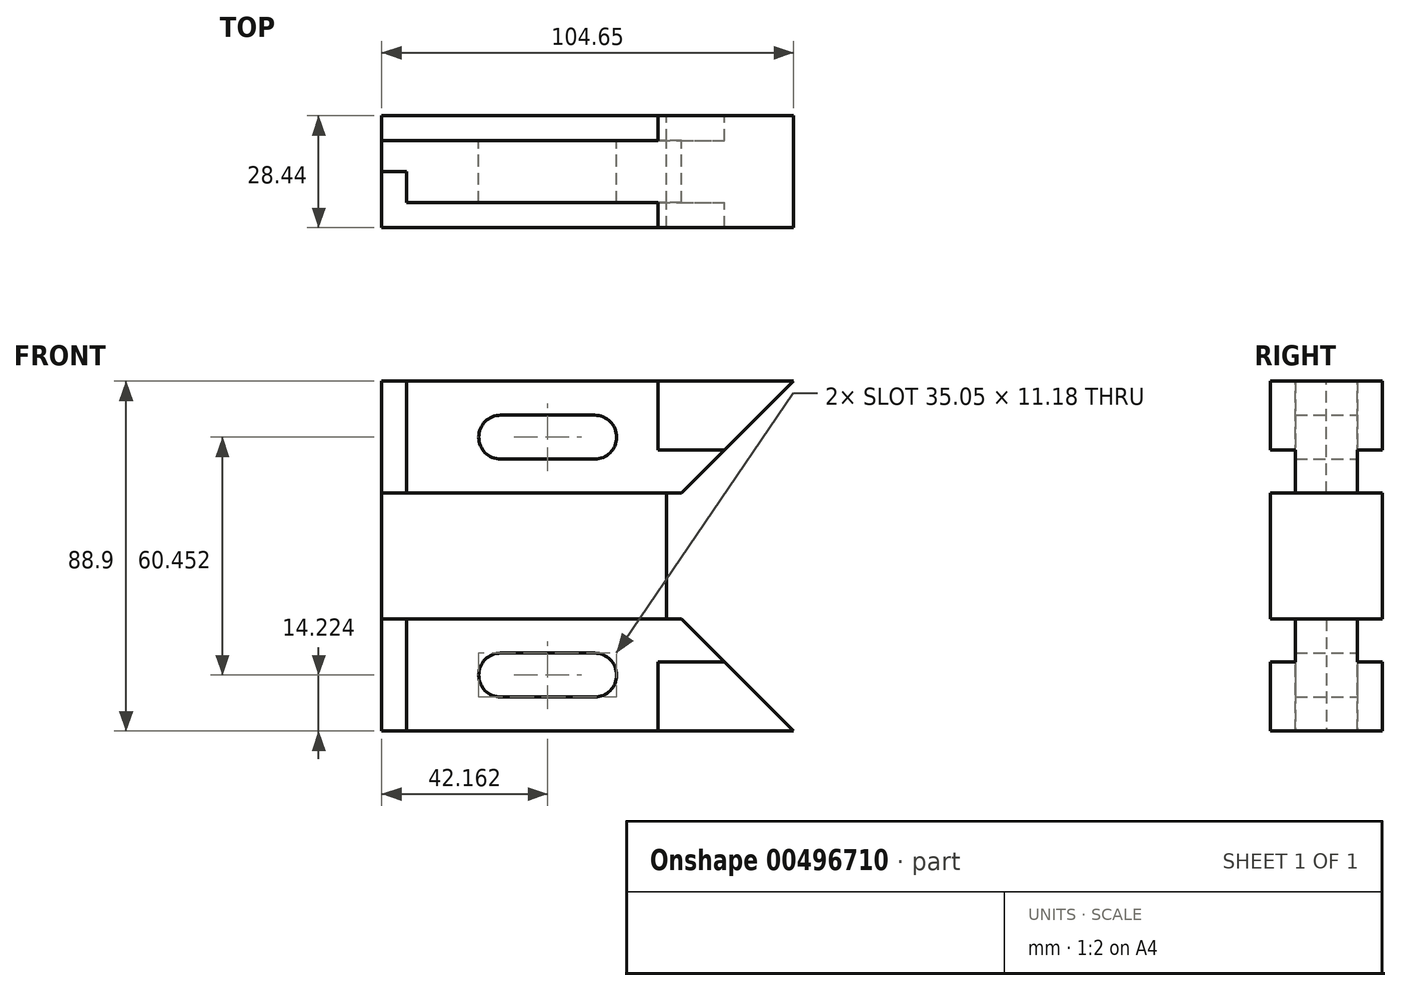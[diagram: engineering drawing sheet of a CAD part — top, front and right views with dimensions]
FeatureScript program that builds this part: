
annotation { "Feature Type Name" : "Feature", "Feature Type Description" : "" }
export const myFeature = defineFeature(function(context is Context, id is Id, definition is map)
    precondition{}
    {
        {
            var Q0;
            Q0=qCreatedBy(makeId("Front.planeOp"),FACE);
            var sketch = newSketch(context, id + "F0", { "sketchPlane" : qUnion([Q0])});
            skLineSegment(sketch, "E0.MirrorCS", {"start": v(-0.76, 16) * mm, "end": v(-76.96, 16) * mm});
            skLineSegment(sketch, "E1.MirrorCS", {"start": v(-76.96, 16) * mm, "end": v(-76.96, 44.45) * mm});
            skLineSegment(sketch, "E2.MirrorCS", {"start": v(-0.76, 16) * mm, "end": v(27.69, 44.45) * mm});
            skLineSegment(sketch, "E3.MirrorCS", {"start": v(-70.61, 16) * mm, "end": v(-70.61, 44.45) * mm});
            skLineSegment(sketch, "E4.MirrorCS", {"start": v(-76.96, 44.45) * mm, "end": v(27.69, 44.45) * mm});
            skLineSegment(sketch, "E5", {"start": v(-76.96, 30.23) * mm, "end": v(-76.96, 30.23) * mm});
            skPoint(sketch, "E5.endSnap0", {"position": v(-76.96, 30.23) * mm});
            skArc(sketch, "E6", {"start": v(-22.86, 24.64) * mm, "mid": v(-17.27, 30.23) * mm, "end": v(-22.86, 35.81) * mm});
            skArc(sketch, "E7", {"start": v(-46.74, 35.81) * mm, "mid": v(-52.32, 30.23) * mm, "end": v(-46.74, 24.64) * mm});
            skLineSegment(sketch, "E8", {"start": v(-46.74, 35.81) * mm, "end": v(-22.86, 35.81) * mm});
            skLineSegment(sketch, "E9", {"start": v(-22.86, 24.64) * mm, "end": v(-46.74, 24.64) * mm});
            skLineSegment(sketch, "E10", {"start": v(-6.72, 44.45) * mm, "end": v(-6.72, 26.92) * mm});
            skLineSegment(sketch, "E11", {"start": v(-6.72, 26.92) * mm, "end": v(10.16, 26.92) * mm});
            skPoint(sketch, "E12.MirrorP", {"position": v(-76.96, -30.23) * mm});
            skLineSegment(sketch, "E13.MirrorCS", {"start": v(-46.74, -35.81) * mm, "end": v(-22.86, -35.81) * mm});
            skArc(sketch, "E14.MirrorC", {"start": v(-46.74, -35.81) * mm, "mid": v(-52.32, -30.23) * mm, "end": v(-46.74, -24.64) * mm});
            skLineSegment(sketch, "E15.MirrorCS", {"start": v(-70.61, -16) * mm, "end": v(-70.61, -44.45) * mm});
            skLineSegment(sketch, "E16.MirrorCS", {"start": v(-0.76, -16) * mm, "end": v(27.69, -44.45) * mm});
            skLineSegment(sketch, "E17.MirrorCS", {"start": v(-76.96, -16) * mm, "end": v(-76.96, -44.45) * mm});
            skLineSegment(sketch, "E18.MirrorCS", {"start": v(-22.86, -24.64) * mm, "end": v(-46.74, -24.64) * mm});
            skArc(sketch, "E19.MirrorC", {"start": v(-22.86, -24.64) * mm, "mid": v(-17.27, -30.23) * mm, "end": v(-22.86, -35.81) * mm});
            skLineSegment(sketch, "E20.MirrorCS", {"start": v(-76.96, -30.23) * mm, "end": v(-76.96, -30.23) * mm});
            skLineSegment(sketch, "E21.MirrorCS", {"start": v(-6.72, -44.45) * mm, "end": v(-6.72, -26.92) * mm});
            skLineSegment(sketch, "E22.MirrorCS", {"start": v(-0.76, -16) * mm, "end": v(-76.96, -16) * mm});
            skLineSegment(sketch, "E23.MirrorCS", {"start": v(-6.72, -26.92) * mm, "end": v(10.16, -26.92) * mm});
            skLineSegment(sketch, "E24.MirrorCS", {"start": v(-76.96, -44.45) * mm, "end": v(27.69, -44.45) * mm});
            skLineSegment(sketch, "E25", {"start": v(-76.96, 16) * mm, "end": v(-76.96, -16) * mm});
            skLineSegment(sketch, "E26", {"start": v(-4.57, 16) * mm, "end": v(-4.57, -16) * mm});
            skSolve(sketch);
        }
        {
            var Q0;
            {var subQ2=sQuery(id+"F0.wireOp",EDGE,"E25");Q0=makeQuery(id+"F0.imprint","IMPRINT",FACE,{"disambiguationData":[TD([[makeQuery(id+"F0.imprint","IMPRINT",EDGE,{"derivedFrom":subQ2}),1.0]])]});}
            extrude(context, id + "F1", {"entities" : qUnion([Q0]), "depth" : 28.45 * mm, "symmetric" : true});
        }
        {
            var Q0;
            {var subQ2=sQuery(id+"F0.wireOp",EDGE,"E3.MirrorCS");Q0=makeQuery(id+"F0.imprint","IMPRINT",FACE,{"disambiguationData":[TD([[makeQuery(id+"F0.imprint","IMPRINT",EDGE,{"derivedFrom":subQ2}),-1.0]])]});}
            var Q1;
            Q1=makeQuery(id+"F0.imprint","IMPRINT",FACE,{"disambiguationData":[TD([[makeQuery(id+"F0.imprint","IMPRINT",EDGE,{"derivedFrom":sQuery(id+"F0.wireOp",EDGE,"E13.MirrorCS")}),-1.0]])]});
            extrude(context, id + "F2", {"entities" : qUnion([Q0, Q1]), "operationType" : NewBodyOperationType.ADD, "depth" : 15.75 * mm, "offsetDistance" : 25.4 * mm, "symmetric" : true});
        }
        {
            var Q0;
            {var subQ4=sQuery(id+"F0.wireOp",EDGE,"E21.MirrorCS");Q0=makeQuery(id+"F0.imprint","IMPRINT",FACE,{"disambiguationData":[TD([[makeQuery(id+"F0.imprint","IMPRINT",EDGE,{"derivedFrom":subQ4}),-1.0]])]});}
            var Q1;
            {var subQ4=sQuery(id+"F0.wireOp",EDGE,"E10");Q1=makeQuery(id+"F0.imprint","IMPRINT",FACE,{"disambiguationData":[TD([[makeQuery(id+"F0.imprint","IMPRINT",EDGE,{"derivedFrom":subQ4}),1.0]])]});}
            extrude(context, id + "F3", {"entities" : qUnion([Q0, Q1]), "operationType" : NewBodyOperationType.ADD, "depth" : 28.45 * mm, "offsetDistance" : 25.4 * mm, "symmetric" : true});
        }
        {
            var Q0;
            {var subQ0=sQuery(id+"F0.wireOp",EDGE,"E1.MirrorCS");Q0=makeQuery(id+"F0.imprint","IMPRINT",FACE,{"disambiguationData":[TD([[makeQuery(id+"F0.imprint","IMPRINT",EDGE,{"derivedFrom":subQ0}),-1.0]])]});}
            var Q1;
            {var subQ0=sQuery(id+"F0.wireOp",EDGE,"E15.MirrorCS");Q1=makeQuery(id+"F0.imprint","IMPRINT",FACE,{"disambiguationData":[TD([[makeQuery(id+"F0.imprint","IMPRINT",EDGE,{"derivedFrom":subQ0}),-1.0]])]});}
            extrude(context, id + "F4", {"entities" : qUnion([Q0, Q1]), "operationType" : NewBodyOperationType.ADD, "oppositeDirection" : true, "depth" : 7.87 * mm, "offsetDistance" : 25.4 * mm});
        }
    });
